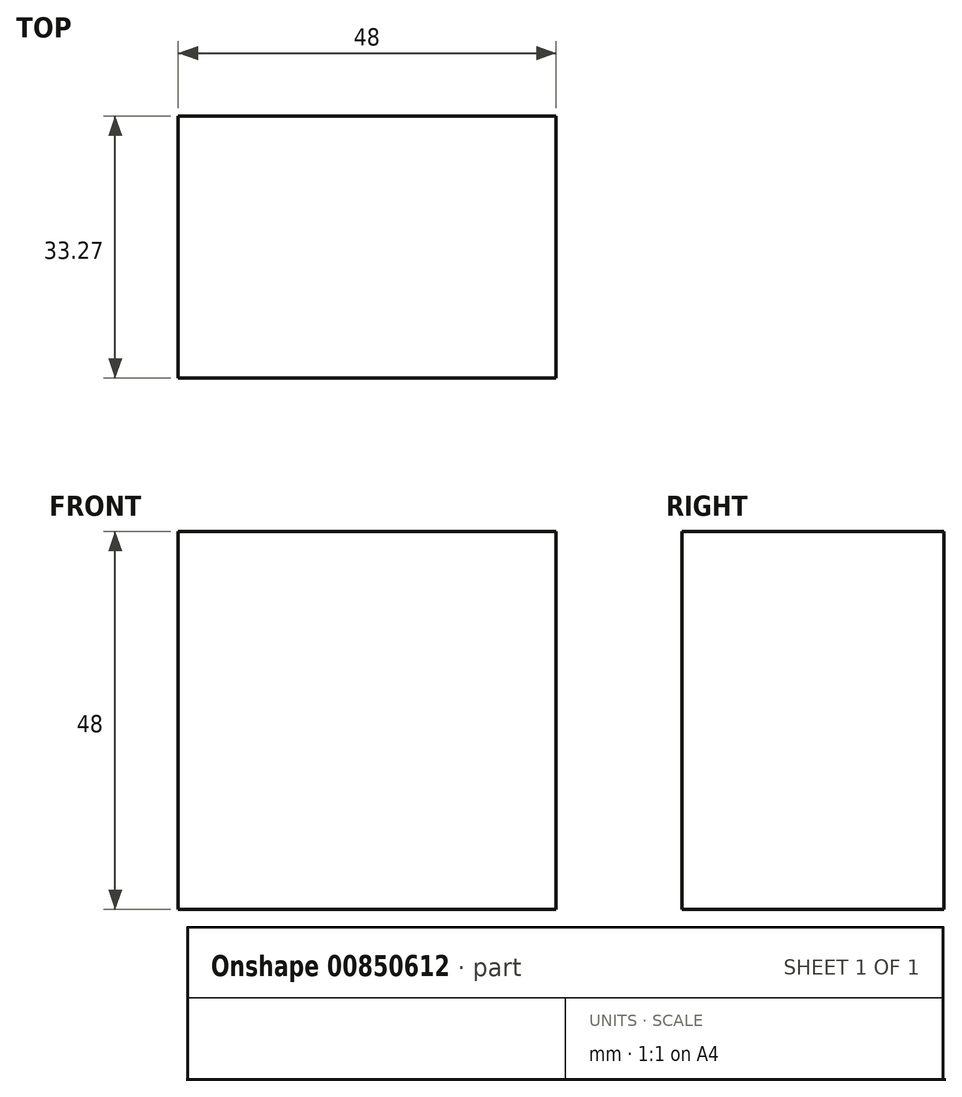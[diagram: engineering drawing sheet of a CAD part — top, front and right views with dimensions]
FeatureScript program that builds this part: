
annotation { "Feature Type Name" : "Feature", "Feature Type Description" : "" }
export const myFeature = defineFeature(function(context is Context, id is Id, definition is map)
    precondition{}
    {
        {
            var Q0;
            Q0=qCreatedBy(makeId("Front.planeOp"),FACE);
            var sketch = newSketch(context, id + "F0", { "sketchPlane" : qUnion([Q0])});
            skLineSegment(sketch, "E0.bottom", {"start": v(-60.35, 22.16) * mm, "end": v(-12.35, 22.16) * mm});
            skLineSegment(sketch, "E0.top", {"start": v(-60.35, -25.84) * mm, "end": v(-12.35, -25.84) * mm});
            skLineSegment(sketch, "E0.left", {"start": v(-60.35, 22.16) * mm, "end": v(-60.35, -25.84) * mm});
            skLineSegment(sketch, "E0.right", {"start": v(-12.35, 22.16) * mm, "end": v(-12.35, -25.84) * mm});
            skSolve(sketch);
        }
        {
            var Q0;
            Q0 = qSketchRegion(id + "F0", true);
            extrude(context, id + "F1", {"entities" : qUnion([Q0]), "depth" : 33.27 * mm, "offsetDistance" : 25.4 * mm});
        }
    });
